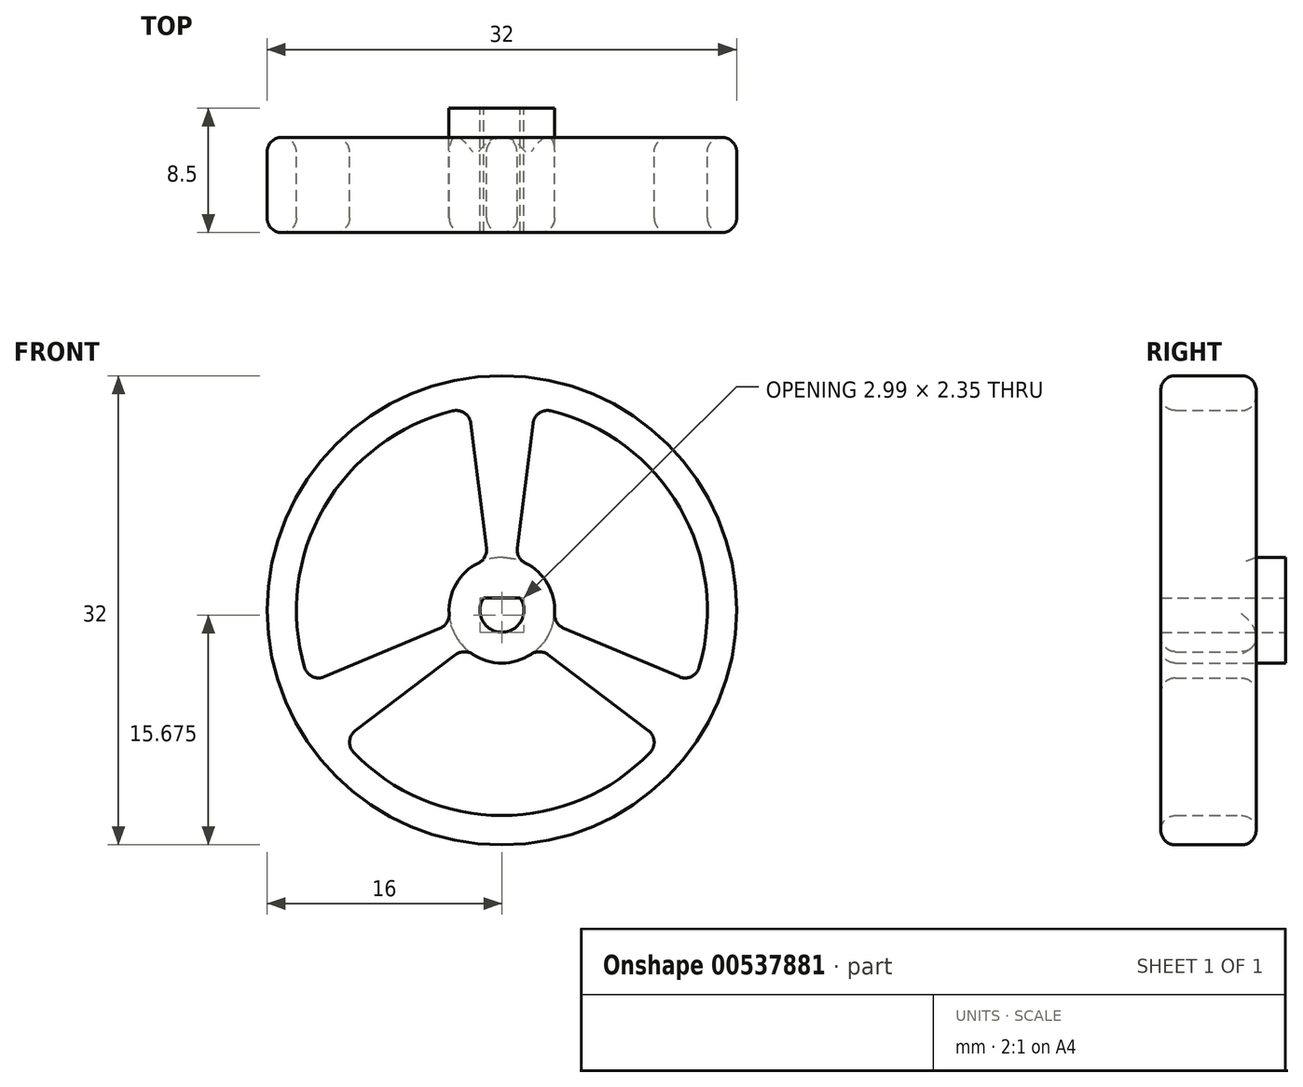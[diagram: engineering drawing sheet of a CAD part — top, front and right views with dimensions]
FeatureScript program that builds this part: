
annotation { "Feature Type Name" : "Feature", "Feature Type Description" : "" }
export const myFeature = defineFeature(function(context is Context, id is Id, definition is map)
    precondition{}
    {
        {
            var Q0;
            Q0=qCreatedBy(makeId("Front.planeOp"),FACE);
            var sketch = newSketch(context, id + "F0", { "sketchPlane" : qUnion([Q0])});
            skCircle(sketch, "E0", {"center": v(0, 0) * mm, "radius": 16 * mm});
            skArc(sketch, "E1", {"start": v(-3.35, 13.6) * mm, "mid": v(-12.12, 7) * mm, "end": v(-13.45, -3.9) * mm});
            skArc(sketch, "E2", {"start": v(-1.6, 3.23) * mm, "mid": v(-3.12, 1.8) * mm, "end": v(-3.6, -0.23) * mm});
            skArc(sketch, "E3", {"start": v(-1.24, 0.85) * mm, "mid": v(0, -1.5) * mm, "end": v(1.24, 0.85) * mm});
            skLineSegment(sketch, "E4", {"start": v(-1.24, 0.85) * mm, "end": v(1.24, 0.85) * mm});
            skPoint(sketch, "E5", {"position": v(0, -1.5) * mm});
            skLineSegment(sketch, "E6", {"start": v(-2.12, 12.75) * mm, "end": v(-1.05, 4.25) * mm});
            skLineSegment(sketch, "E7", {"start": v(2.12, 12.75) * mm, "end": v(1.05, 4.25) * mm});
            skLineSegment(sketch, "E8", {"start": v(-4.2, -1.22) * mm, "end": v(-12.1, -4.54) * mm});
            skLineSegment(sketch, "E9", {"start": v(-3.15, -3.03) * mm, "end": v(-9.98, -8.2) * mm});
            skLineSegment(sketch, "E10", {"start": v(4.2, -1.22) * mm, "end": v(12.1, -4.54) * mm});
            skLineSegment(sketch, "E11", {"start": v(3.15, -3.03) * mm, "end": v(9.98, -8.2) * mm});
            skLineSegment(sketch, "E12", {"start": v(-0.95, 3.47) * mm, "end": v(0.95, 3.47) * mm, "construction": true});
            skLineSegment(sketch, "E13", {"start": v(0.95, 3.47) * mm, "end": v(3.48, -0.91) * mm, "construction": true});
            skLineSegment(sketch, "E14", {"start": v(3.48, -0.91) * mm, "end": v(2.53, -2.56) * mm, "construction": true});
            skLineSegment(sketch, "E15", {"start": v(2.53, -2.56) * mm, "end": v(-2.53, -2.56) * mm, "construction": true});
            skLineSegment(sketch, "E16", {"start": v(-2.53, -2.56) * mm, "end": v(-3.48, -0.91) * mm, "construction": true});
            skLineSegment(sketch, "E17", {"start": v(-3.48, -0.91) * mm, "end": v(-0.95, 3.47) * mm, "construction": true});
            skPoint(sketch, "E18", {"position": v(0, 3.47) * mm});
            skLineSegment(sketch, "E19", {"start": v(-2.25, 13.82) * mm, "end": v(2.25, 13.82) * mm, "construction": true});
            skLineSegment(sketch, "E20", {"start": v(2.25, 13.82) * mm, "end": v(13.1, -4.96) * mm, "construction": true});
            skLineSegment(sketch, "E21", {"start": v(13.1, -4.96) * mm, "end": v(10.84, -8.86) * mm, "construction": true});
            skLineSegment(sketch, "E22", {"start": v(10.84, -8.86) * mm, "end": v(-10.84, -8.86) * mm, "construction": true});
            skLineSegment(sketch, "E23", {"start": v(-10.84, -8.86) * mm, "end": v(-13.1, -4.96) * mm, "construction": true});
            skLineSegment(sketch, "E24", {"start": v(-13.1, -4.96) * mm, "end": v(-2.25, 13.82) * mm, "construction": true});
            skPoint(sketch, "E25", {"position": v(0, 13.82) * mm});
            skArc(sketch, "E26.trimOffspring", {"start": v(-2, -3) * mm, "mid": v(0, -3.6) * mm, "end": v(2, -3) * mm});
            skArc(sketch, "E27.trimOffspring", {"start": v(3.6, -0.23) * mm, "mid": v(3.12, 1.8) * mm, "end": v(1.6, 3.23) * mm});
            skArc(sketch, "E28.trimOffspring", {"start": v(13.45, -3.9) * mm, "mid": v(12.12, 7) * mm, "end": v(3.35, 13.6) * mm});
            skArc(sketch, "E29.trimOffspring", {"start": v(-10.1, -9.7) * mm, "mid": v(0, -14) * mm, "end": v(10.1, -9.7) * mm});
            skPoint(sketch, "E30.visualSharp", {"position": v(-2.25, 13.82) * mm});
            skArc(sketch, "E30.filletArc", {"start": v(-2.12, 12.75) * mm, "mid": v(-2.54, 13.45) * mm, "end": v(-3.35, 13.6) * mm});
            skPoint(sketch, "E31.visualSharp", {"position": v(2.25, 13.82) * mm});
            skArc(sketch, "E31.filletArc", {"start": v(3.35, 13.6) * mm, "mid": v(2.54, 13.45) * mm, "end": v(2.12, 12.75) * mm});
            skPoint(sketch, "E32.visualSharp", {"position": v(13.1, -4.96) * mm});
            skArc(sketch, "E32.filletArc", {"start": v(12.1, -4.54) * mm, "mid": v(12.92, -4.52) * mm, "end": v(13.45, -3.9) * mm});
            skPoint(sketch, "E33.visualSharp", {"position": v(10.84, -8.86) * mm});
            skArc(sketch, "E33.filletArc", {"start": v(10.1, -9.7) * mm, "mid": v(10.37, -8.92) * mm, "end": v(9.98, -8.2) * mm});
            skPoint(sketch, "E34.visualSharp", {"position": v(3.48, -0.91) * mm});
            skArc(sketch, "E34.filletArc", {"start": v(3.6, -0.23) * mm, "mid": v(3.74, -0.82) * mm, "end": v(4.2, -1.22) * mm});
            skPoint(sketch, "E35.visualSharp", {"position": v(0.95, 3.47) * mm});
            skArc(sketch, "E35.filletArc", {"start": v(1.05, 4.25) * mm, "mid": v(1.16, 3.65) * mm, "end": v(1.6, 3.23) * mm});
            skPoint(sketch, "E36.visualSharp", {"position": v(-0.95, 3.47) * mm});
            skArc(sketch, "E36.filletArc", {"start": v(-1.6, 3.23) * mm, "mid": v(-1.16, 3.65) * mm, "end": v(-1.05, 4.25) * mm});
            skPoint(sketch, "E37.visualSharp", {"position": v(-3.48, -0.91) * mm});
            skArc(sketch, "E37.filletArc", {"start": v(-4.2, -1.22) * mm, "mid": v(-3.74, -0.82) * mm, "end": v(-3.6, -0.23) * mm});
            skPoint(sketch, "E38.visualSharp", {"position": v(-2.53, -2.56) * mm});
            skArc(sketch, "E38.filletArc", {"start": v(-2, -3) * mm, "mid": v(-2.58, -2.83) * mm, "end": v(-3.15, -3.03) * mm});
            skPoint(sketch, "E39.visualSharp", {"position": v(2.53, -2.56) * mm});
            skArc(sketch, "E39.filletArc", {"start": v(3.15, -3.03) * mm, "mid": v(2.58, -2.83) * mm, "end": v(2, -3) * mm});
            skPoint(sketch, "E40.visualSharp", {"position": v(-10.84, -8.86) * mm});
            skArc(sketch, "E40.filletArc", {"start": v(-9.98, -8.2) * mm, "mid": v(-10.37, -8.92) * mm, "end": v(-10.1, -9.7) * mm});
            skPoint(sketch, "E41.visualSharp", {"position": v(-13.1, -4.96) * mm});
            skArc(sketch, "E41.filletArc", {"start": v(-13.45, -3.9) * mm, "mid": v(-12.92, -4.52) * mm, "end": v(-12.1, -4.54) * mm});
            skSolve(sketch);
        }
        {
            var Q0;
            Q0=makeQuery(id+"F0.imprint","IMPRINT",FACE,{"disambiguationData":[TD([[makeQuery(id+"F0.imprint","IMPRINT",EDGE,{"derivedFrom":sQuery(id+"F0.wireOp",EDGE,"E0")}),1.0]])]});
            extrude(context, id + "F1", {"entities" : qUnion([Q0]), "endBound" : BoundingType.SYMMETRIC, "depth" : 6.5 * mm, "offsetDistance" : 25 * mm});
        }
        {
            var Q0;
            Q0=makeQuery(id+"F1.opExtrude","CAP_FACE",FACE,{"disambiguationData":[OSD([sQuery(id+"F0.wireOp",EDGE,"E0"),sQuery(id+"F0.wireOp",EDGE,"E1"),sQuery(id+"F0.wireOp",EDGE,"E2"),sQuery(id+"F0.wireOp",EDGE,"E3"),sQuery(id+"F0.wireOp",EDGE,"E4"),sQuery(id+"F0.wireOp",EDGE,"E6"),sQuery(id+"F0.wireOp",EDGE,"E7"),sQuery(id+"F0.wireOp",EDGE,"E8"),sQuery(id+"F0.wireOp",EDGE,"E9"),sQuery(id+"F0.wireOp",EDGE,"E10"),sQuery(id+"F0.wireOp",EDGE,"E11"),sQuery(id+"F0.wireOp",EDGE,"E26.trimOffspring"),sQuery(id+"F0.wireOp",EDGE,"E27.trimOffspring"),sQuery(id+"F0.wireOp",EDGE,"E28.trimOffspring"),sQuery(id+"F0.wireOp",EDGE,"E29.trimOffspring"),sQuery(id+"F0.wireOp",EDGE,"E30.filletArc"),sQuery(id+"F0.wireOp",EDGE,"E31.filletArc"),sQuery(id+"F0.wireOp",EDGE,"E32.filletArc"),sQuery(id+"F0.wireOp",EDGE,"E33.filletArc"),sQuery(id+"F0.wireOp",EDGE,"E34.filletArc"),sQuery(id+"F0.wireOp",EDGE,"E35.filletArc"),sQuery(id+"F0.wireOp",EDGE,"E36.filletArc"),sQuery(id+"F0.wireOp",EDGE,"E37.filletArc"),sQuery(id+"F0.wireOp",EDGE,"E38.filletArc"),sQuery(id+"F0.wireOp",EDGE,"E39.filletArc"),sQuery(id+"F0.wireOp",EDGE,"E40.filletArc"),sQuery(id+"F0.wireOp",EDGE,"E41.filletArc")])],"isStart":true});
            var sketch = newSketch(context, id + "F2", { "sketchPlane" : qUnion([Q0])});
            skArc(sketch, "E42.0", {"start": v(-3.6, -0.23) * mm, "mid": v(-3.12, 1.8) * mm, "end": v(-1.6, 3.23) * mm});
            skArc(sketch, "E43.0", {"start": v(1.6, 3.23) * mm, "mid": v(3.12, 1.8) * mm, "end": v(3.6, -0.23) * mm});
            skArc(sketch, "E44.0", {"start": v(2, -3) * mm, "mid": v(0, -3.6) * mm, "end": v(-2, -3) * mm});
            skArc(sketch, "E45.0", {"start": v(1.24, 0.85) * mm, "mid": v(0, -1.5) * mm, "end": v(-1.24, 0.85) * mm});
            skLineSegment(sketch, "E46.0", {"start": v(1.24, 0.85) * mm, "end": v(-1.24, 0.85) * mm});
            skCircle(sketch, "E47", {"center": v(0, 0) * mm, "radius": 3.6 * mm});
            skSolve(sketch);
        }
        {
            var Q0;
            Q0=makeQuery(id+"F2.imprint","IMPRINT",FACE,{"disambiguationData":[TD([[makeQuery(id+"F2.imprint","IMPRINT",EDGE,{"derivedFrom":sQuery(id+"F2.wireOp",EDGE,"E45.0")}),1.0]])]});
            extrude(context, id + "F3", {"entities" : qUnion([Q0]), "operationType" : NewBodyOperationType.ADD, "depth" : 2 * mm, "offsetDistance" : 25 * mm});
        }
        {
            var Q0;
            Q0=makeQuery(id+"F1.opExtrude","SWEPT_FACE",FACE,{"disambiguationData":[OSD([sQuery(id+"F0.wireOp",EDGE,"E0")])]});
            var Q1;
            Q1=makeQuery(id+"F1.opExtrude","SWEPT_FACE",FACE,{"disambiguationData":[OSD([sQuery(id+"F0.wireOp",EDGE,"E28.trimOffspring")])]});
            var Q2;
            Q2=makeQuery(id+"F1.opExtrude","SWEPT_FACE",FACE,{"disambiguationData":[OSD([sQuery(id+"F0.wireOp",EDGE,"E6")])]});
            var Q3;
            Q3=makeQuery(id+"F1.opExtrude","SWEPT_FACE",FACE,{"disambiguationData":[OSD([sQuery(id+"F0.wireOp",EDGE,"E11")])]});
            fillet(context, id + "F4", {"entities" : qUnion([Q0, Q1, Q2, Q3]), "radius" : 1 * mm, "tangentPropagation" : true, "allowEdgeOverflow" : false});
        }
    });
